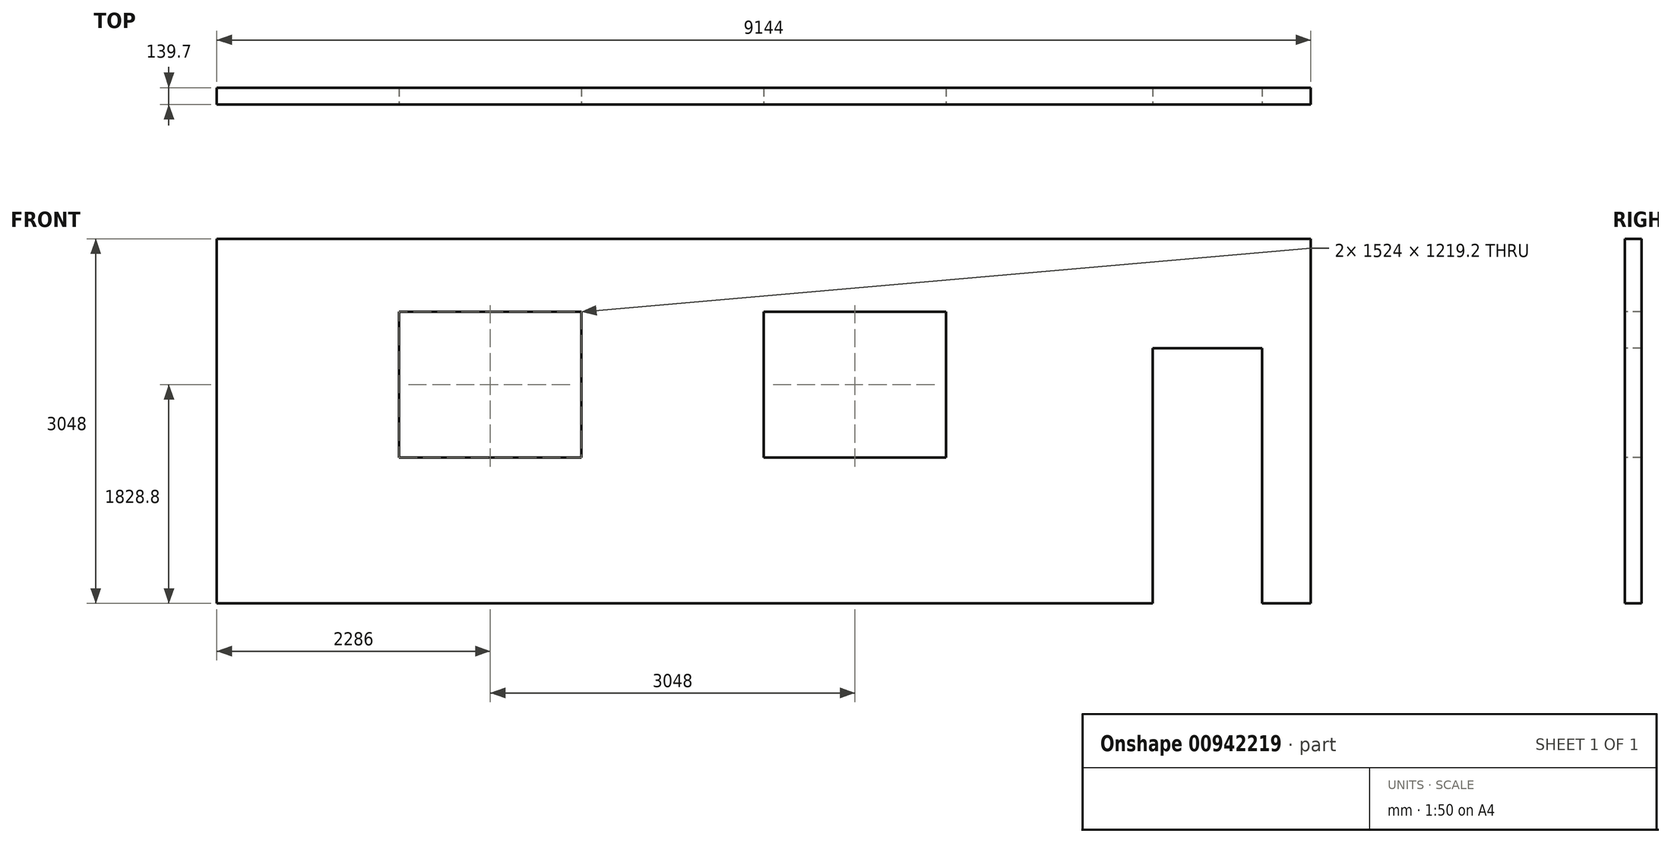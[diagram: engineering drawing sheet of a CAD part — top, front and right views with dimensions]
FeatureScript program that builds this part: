
annotation { "Feature Type Name" : "Feature", "Feature Type Description" : "" }
export const myFeature = defineFeature(function(context is Context, id is Id, definition is map)
    precondition{}
    {
        {
            var Q0;
            Q0=qCreatedBy(makeId("Front.planeOp"),FACE);
            var sketch = newSketch(context, id + "F0", { "sketchPlane" : qUnion([Q0])});
            skLineSegment(sketch, "E0.bottom", {"start": v(0, 0) * mm, "end": v(9144, 0) * mm});
            skLineSegment(sketch, "E0.top", {"start": v(0, 3048) * mm, "end": v(9144, 3048) * mm});
            skLineSegment(sketch, "E0.left", {"start": v(0, 0) * mm, "end": v(0, 3048) * mm});
            skLineSegment(sketch, "E0.right", {"start": v(9144, 0) * mm, "end": v(9144, 3048) * mm});
            skSolve(sketch);
        }
        {
            var Q0;
            Q0=makeQuery(id+"F0.imprint","IMPRINT",FACE,{"disambiguationData":[TD([[makeQuery(id+"F0.imprint","IMPRINT",EDGE,{"derivedFrom":sQuery(id+"F0.wireOp",EDGE,"E0.bottom")}),1.0]])]});
            extrude(context, id + "F1", {"entities" : qUnion([Q0]), "oppositeDirection" : true, "depth" : 139.7 * mm, "offsetDistance" : 25.4 * mm});
        }
        {
            var Q0;
            Q0=makeQuery(id+"F1.opExtrude","CAP_FACE",FACE,{"disambiguationData":[OSD([sQuery(id+"F0.wireOp",EDGE,"E0.bottom"),sQuery(id+"F0.wireOp",EDGE,"E0.top"),sQuery(id+"F0.wireOp",EDGE,"E0.left"),sQuery(id+"F0.wireOp",EDGE,"E0.right")])],"isStart":true});
            var sketch = newSketch(context, id + "F2", { "sketchPlane" : qUnion([Q0])});
            skLineSegment(sketch, "E1.bottom", {"start": v(1524, 2438.4) * mm, "end": v(3048, 2438.4) * mm});
            skLineSegment(sketch, "E1.top", {"start": v(1524, 1219.2) * mm, "end": v(3048, 1219.2) * mm});
            skLineSegment(sketch, "E1.left", {"start": v(1524, 2438.4) * mm, "end": v(1524, 1219.2) * mm});
            skLineSegment(sketch, "E1.right", {"start": v(3048, 2438.4) * mm, "end": v(3048, 1219.2) * mm});
            skLineSegment(sketch, "E2.bottom", {"start": v(4572, 2438.4) * mm, "end": v(6096, 2438.4) * mm});
            skLineSegment(sketch, "E2.top", {"start": v(4572, 1219.2) * mm, "end": v(6096, 1219.2) * mm});
            skLineSegment(sketch, "E2.left", {"start": v(4572, 2438.4) * mm, "end": v(4572, 1219.2) * mm});
            skLineSegment(sketch, "E2.right", {"start": v(6096, 2438.4) * mm, "end": v(6096, 1219.2) * mm});
            skSolve(sketch);
        }
        {
            var Q0;
            Q0=makeQuery(id+"F2.imprint","IMPRINT",FACE,{"disambiguationData":[TD([[makeQuery(id+"F2.imprint","IMPRINT",EDGE,{"derivedFrom":sQuery(id+"F2.wireOp",EDGE,"E1.bottom")}),-1.0]])]});
            var Q1;
            Q1=makeQuery(id+"F2.imprint","IMPRINT",FACE,{"disambiguationData":[TD([[makeQuery(id+"F2.imprint","IMPRINT",EDGE,{"derivedFrom":sQuery(id+"F2.wireOp",EDGE,"E2.bottom")}),-1.0]])]});
            extrude(context, id + "F3", {"entities" : qUnion([Q0, Q1]), "operationType" : NewBodyOperationType.REMOVE, "endBound" : BoundingType.THROUGH_ALL, "oppositeDirection" : true, "depth" : 25.4 * mm, "offsetDistance" : 25.4 * mm});
        }
        {
            var Q0;
            Q0=makeQuery(id+"F1.opExtrude","CAP_FACE",FACE,{"disambiguationData":[OSD([sQuery(id+"F0.wireOp",EDGE,"E0.bottom"),sQuery(id+"F0.wireOp",EDGE,"E0.top"),sQuery(id+"F0.wireOp",EDGE,"E0.left"),sQuery(id+"F0.wireOp",EDGE,"E0.right")])],"isStart":true});
            var sketch = newSketch(context, id + "F4", { "sketchPlane" : qUnion([Q0])});
            skLineSegment(sketch, "E3.bottom", {"start": v(7823.2, 0) * mm, "end": v(8737.6, 0) * mm});
            skLineSegment(sketch, "E3.top", {"start": v(7823.2, 2133.6) * mm, "end": v(8737.6, 2133.6) * mm});
            skLineSegment(sketch, "E3.left", {"start": v(7823.2, 0) * mm, "end": v(7823.2, 2133.6) * mm});
            skLineSegment(sketch, "E3.right", {"start": v(8737.6, 0) * mm, "end": v(8737.6, 2133.6) * mm});
            skSolve(sketch);
        }
        {
            var Q0;
            Q0=makeQuery(id+"F4.imprint","IMPRINT",FACE,{"disambiguationData":[TD([[makeQuery(id+"F4.imprint","IMPRINT",EDGE,{"derivedFrom":sQuery(id+"F4.wireOp",EDGE,"E3.bottom")}),1.0]])]});
            extrude(context, id + "F5", {"entities" : qUnion([Q0]), "operationType" : NewBodyOperationType.REMOVE, "endBound" : BoundingType.THROUGH_ALL, "oppositeDirection" : true, "depth" : 25.4 * mm, "offsetDistance" : 25.4 * mm});
        }
    });
